# Revit family: Domotics-DomesticRanges-GEWISS-SYSTEM_COMMAND-INTERMEDIATE_SWITCH
name_source: partatom
category: Apparecchi elettrici
revit_build: Autodesk Revit 2016 (Build: 20161004_0715(x64)
units: mm (PartAtom-declared; Revit-internal decimal feet)

## family parameters
Condiviso = Sì
Host = Superficie
Mantenere orientamento annotazione = Sì
Numero OmniClass = 23.80.50.11.14
Punto di calcolo locali = Sì
Quota connettore circolare = Usa diametro
Taglio con vuoti quando caricato = No
Tipo di parte = Normale
Titolo OmniClass = Switches

## types (2) — shared parameters
Button key = Neutral
Carico apparente = 0 VA
Catalogue = DOMOTICS
Catalogue Range = SYSTEM - DOMESTIC RANGE
Description. = Intermediate switch
Description: = 1P - 16AX
Electrocod = 0130
IDF = 10cd831b-a85d-4ab1-b98b-127a7fbad0b2
IDT = af7ce9fa-211b-4075-b059-875f33530734
Immagine tipo = GW21579.jpg
Larghezza pulsante = 23 mm  [stored 0.0754593 ft]
N. poli = 1
No. SYSTEM modules = 1
Produttore = GEWISS S.p.A.
Prospetto di default = 1219 mm
SEO = Intermediate switch
Simbolo = SIMBOLO INVERTITORI : INV1P
Technical sheet = https://www.gewiss.com
Tipo_ = SYSTEM INVERTITORI_BASE : NERO
Type = General
URL = https://www.gewiss.com
Version file RFA = 19.4
Volt = 230 V
Voltage = 250 V ac
Voltage: = 250 V ac

## per-type parameters (varying)
| type | Colour | Descrizione | EAN code | Modello |
| GW20579 - Rev.-switch-16Ax white | White | REV.-SWITCH-16AX SY/WT | 8011564132993 | GW20579 |
| GW21579 - Rev.-switch-16Ax black | Black | REV.-SWITCH-16AX SY/BK | 8011564133075 | GW21579 |

note: [stored X ft] marks values corroborated as IEEE doubles in the binary element streams (Revit-internal decimal feet)

## geometry (parser evidence)
native form markers: Sweep x1
no freeform markers — native parametric forms only
